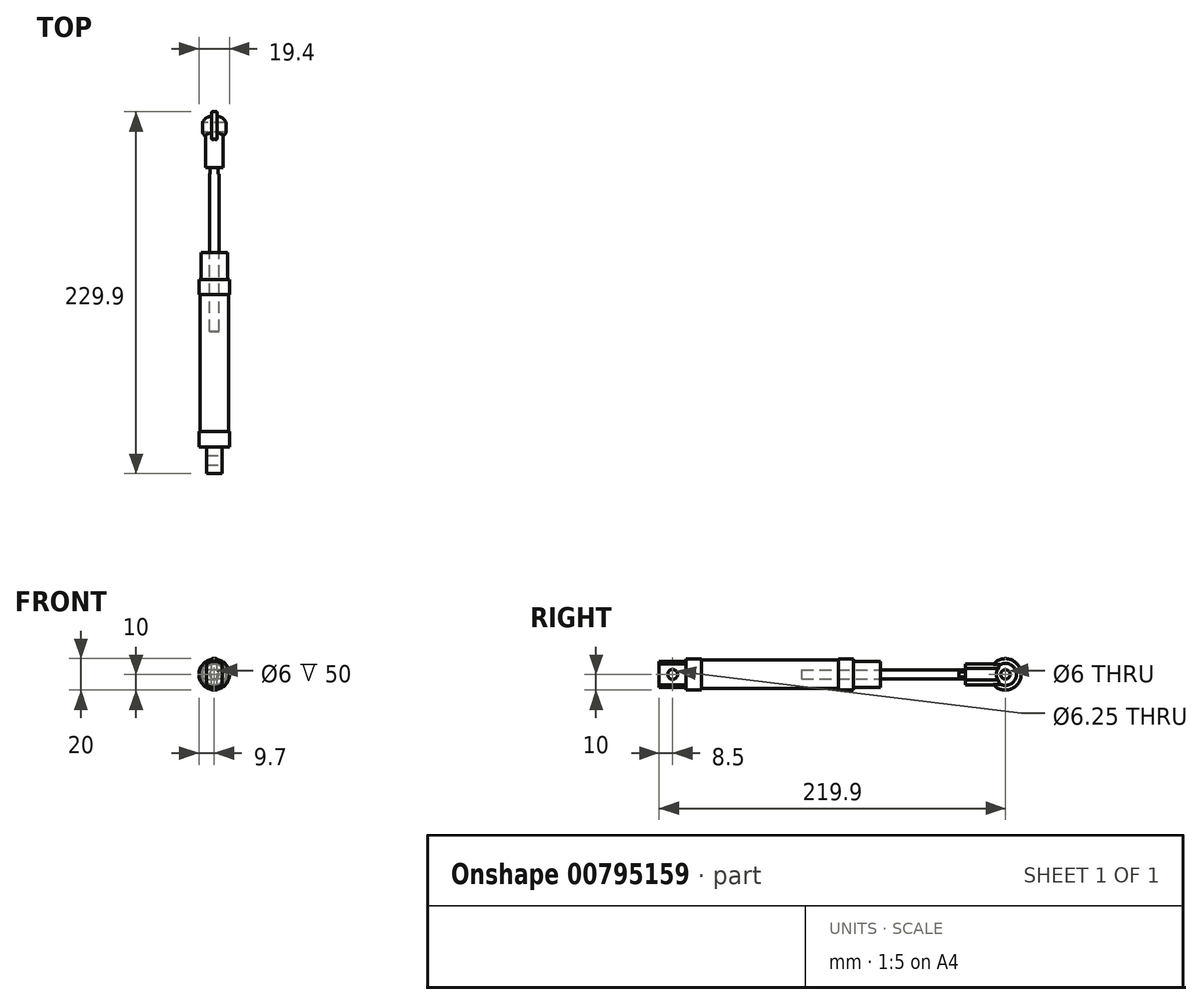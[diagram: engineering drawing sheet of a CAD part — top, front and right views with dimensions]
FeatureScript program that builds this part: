
annotation { "Feature Type Name" : "Feature", "Feature Type Description" : "" }
export const myFeature = defineFeature(function(context is Context, id is Id, definition is map)
    precondition{}
    {
        {
            var Q0;
            Q0=qCreatedBy(makeId("Front.planeOp"),FACE);
            var sketch = newSketch(context, id + "F0", { "sketchPlane" : qUnion([Q0])});
            skCircle(sketch, "E0", {"center": v(0, 0) * mm, "radius": 8.32 * mm});
            skSolve(sketch);
        }
        {
            var Q0;
            Q0=makeQuery(id+"F0.imprint","IMPRINT",FACE,{"disambiguationData":[TD([[makeQuery(id+"F0.imprint","IMPRINT",EDGE,{"derivedFrom":sQuery(id+"F0.wireOp",EDGE,"E0")}),1.0]])]});
            extrude(context, id + "F1", {"entities" : qUnion([Q0]), "depth" : 17 * mm, "offsetDistance" : 25 * mm});
        }
        {
            var Q0;
            Q0=makeQuery(id+"F1.opExtrude","CAP_FACE",FACE,{"disambiguationData":[OSD([sQuery(id+"F0.wireOp",EDGE,"E0")])],"isStart":false});
            var sketch = newSketch(context, id + "F2", { "sketchPlane" : qUnion([Q0])});
            skCircle(sketch, "E1", {"center": v(0, 0) * mm, "radius": 9.7 * mm});
            skSolve(sketch);
        }
        {
            var Q0;
            Q0=makeQuery(id+"F2.imprint","IMPRINT",FACE,{"disambiguationData":[TD([[makeQuery(id+"F2.imprint","IMPRINT",EDGE,{"derivedFrom":sQuery(id+"F2.wireOp",EDGE,"E1")}),1.0]])]});
            var Q1;
            Q1=makeQuery(id+"F2.imprint","IMPRINT",FACE,{"disambiguationData":[TD([[makeQuery(id+"F2.imprint","IMPRINT",EDGE,{"derivedFrom":makeQuery(id+"F1.opExtrude","CAP_EDGE",EDGE,{"disambiguationData":[OSD([sQuery(id+"F0.wireOp",EDGE,"E0")])],"isStart":false})}),1.0]])]});
            extrude(context, id + "F3", {"entities" : qUnion([Q0, Q1]), "operationType" : NewBodyOperationType.ADD, "depth" : 9.65 * mm, "offsetDistance" : 25 * mm});
        }
        {
            var Q0;
            Q0=makeQuery(id+"F3.opExtrude","CAP_FACE",FACE,{"disambiguationData":[OSD([sQuery(id+"F2.wireOp",EDGE,"E1")])],"isStart":false});
            var sketch = newSketch(context, id + "F4", { "sketchPlane" : qUnion([Q0])});
            skCircle(sketch, "E2", {"center": v(0, 0) * mm, "radius": 9.05 * mm});
            skSolve(sketch);
        }
        {
            var Q0;
            Q0=makeQuery(id+"F4.imprint","IMPRINT",FACE,{"disambiguationData":[TD([[makeQuery(id+"F4.imprint","IMPRINT",EDGE,{"derivedFrom":sQuery(id+"F4.wireOp",EDGE,"E2")}),1.0]])]});
            extrude(context, id + "F5", {"entities" : qUnion([Q0]), "operationType" : NewBodyOperationType.ADD, "depth" : 87 * mm, "offsetDistance" : 25 * mm});
        }
        {
            var Q0;
            Q0=makeQuery(id+"F5.opExtrude","CAP_FACE",FACE,{"disambiguationData":[OSD([sQuery(id+"F4.wireOp",EDGE,"E2")])],"isStart":false});
            var sketch = newSketch(context, id + "F6", { "sketchPlane" : qUnion([Q0])});
            skCircle(sketch, "E3", {"center": v(0, 0) * mm, "radius": 9.7 * mm});
            skSolve(sketch);
        }
        {
            var Q0;
            Q0=makeQuery(id+"F6.imprint","IMPRINT",FACE,{"disambiguationData":[TD([[makeQuery(id+"F6.imprint","IMPRINT",EDGE,{"derivedFrom":makeQuery(id+"F5.opExtrude","CAP_EDGE",EDGE,{"disambiguationData":[OSD([sQuery(id+"F4.wireOp",EDGE,"E2")])],"isStart":false})}),1.0]])]});
            var Q1;
            Q1=makeQuery(id+"F6.imprint","IMPRINT",FACE,{"disambiguationData":[TD([[makeQuery(id+"F6.imprint","IMPRINT",EDGE,{"derivedFrom":sQuery(id+"F6.wireOp",EDGE,"E3")}),1.0]])]});
            extrude(context, id + "F7", {"entities" : qUnion([Q0, Q1]), "operationType" : NewBodyOperationType.ADD, "depth" : 9.75 * mm, "offsetDistance" : 25 * mm});
        }
        {
            var Q0;
            Q0=makeQuery(id+"F7.opExtrude","CAP_FACE",FACE,{"disambiguationData":[OSD([sQuery(id+"F6.wireOp",EDGE,"E3")])],"isStart":false});
            var sketch = newSketch(context, id + "F8", { "sketchPlane" : qUnion([Q0])});
            skCircle(sketch, "E4", {"center": v(0, 0) * mm, "radius": 8.32 * mm});
            skSolve(sketch);
        }
        {
            var Q0;
            Q0=makeQuery(id+"F8.imprint","IMPRINT",FACE,{"disambiguationData":[TD([[makeQuery(id+"F8.imprint","IMPRINT",EDGE,{"derivedFrom":sQuery(id+"F8.wireOp",EDGE,"E4")}),1.0]])]});
            extrude(context, id + "F9", {"entities" : qUnion([Q0]), "operationType" : NewBodyOperationType.ADD, "depth" : 17 * mm, "offsetDistance" : 25 * mm});
        }
        {
            var Q0;
            Q0=makeQuery(id+"F1.opExtrude","CAP_FACE",FACE,{"disambiguationData":[OSD([sQuery(id+"F0.wireOp",EDGE,"E0")])],"isStart":true});
            var sketch = newSketch(context, id + "F10", { "sketchPlane" : qUnion([Q0])});
            skCircle(sketch, "E5", {"center": v(0, 0) * mm, "radius": 3 * mm});
            skSolve(sketch);
        }
        {
            var Q0;
            Q0=makeQuery(id+"F10.imprint","IMPRINT",FACE,{"disambiguationData":[TD([[makeQuery(id+"F10.imprint","IMPRINT",EDGE,{"derivedFrom":sQuery(id+"F10.wireOp",EDGE,"E5")}),1.0]])]});
            extrude(context, id + "F11", {"entities" : qUnion([Q0]), "operationType" : NewBodyOperationType.REMOVE, "oppositeDirection" : true, "depth" : 50 * mm, "offsetDistance" : 25 * mm});
        }
        {
            var Q0;
            Q0=makeQuery(id+"F1.opExtrude","CAP_FACE",FACE,{"disambiguationData":[OSD([sQuery(id+"F0.wireOp",EDGE,"E0")])],"isStart":true});
            var sketch = newSketch(context, id + "F12", { "sketchPlane" : qUnion([Q0])});
            skCircle(sketch, "E6", {"center": v(0, 0) * mm, "radius": 3 * mm});
            skSolve(sketch);
        }
        {
            var Q0;
            Q0=makeQuery(id+"F12.imprint","IMPRINT",FACE,{"disambiguationData":[TD([[makeQuery(id+"F12.imprint","IMPRINT",EDGE,{"derivedFrom":sQuery(id+"F12.wireOp",EDGE,"E6")}),1.0]])]});
            extrude(context, id + "F13", {"entities" : qUnion([Q0]), "depth" : 50 * mm, "offsetDistance" : 25 * mm});
        }
        {
            var Q0;
            Q0=makeQuery(id+"F13.opExtrude","CAP_FACE",FACE,{"disambiguationData":[OSD([sQuery(id+"F12.wireOp",EDGE,"E6")])],"isStart":false});
            var sketch = newSketch(context, id + "F14", { "sketchPlane" : qUnion([Q0])});
            skCircle(sketch, "E7", {"center": v(0, 0) * mm, "radius": 3 * mm});
            skLineSegment(sketch, "E8", {"start": v(-2.5, 1.65) * mm, "end": v(-2.5, -1.65) * mm});
            skLineSegment(sketch, "E9.MirrorCS", {"start": v(2.5, 1.65) * mm, "end": v(2.5, -1.65) * mm});
            skSolve(sketch);
        }
        {
            var Q0;
            {var subQ0=sQuery(id+"F14.wireOp",EDGE,"E8");Q0=makeQuery(id+"F14.imprint","IMPRINT",FACE,{"disambiguationData":[TD([[makeQuery(id+"F14.imprint","IMPRINT",EDGE,{"derivedFrom":subQ0}),1.0]])]});}
            extrude(context, id + "F15", {"entities" : qUnion([Q0]), "operationType" : NewBodyOperationType.ADD, "depth" : 4 * mm, "offsetDistance" : 25 * mm});
        }
        {
            var Q0;
            Q0=makeQuery(id+"F15.opExtrude","CAP_FACE",FACE,{"disambiguationData":[OSD([sQuery(id+"F14.wireOp",EDGE,"E7"),sQuery(id+"F14.wireOp",EDGE,"E8"),sQuery(id+"F14.wireOp",EDGE,"E9.MirrorCS")])],"isStart":false});
            var sketch = newSketch(context, id + "F16", { "sketchPlane" : qUnion([Q0])});
            skCircle(sketch, "E10", {"center": v(0, 0) * mm, "radius": 6.6 * mm});
            skLineSegment(sketch, "E11", {"start": v(-5.5, 3.65) * mm, "end": v(-5.5, -3.65) * mm});
            skLineSegment(sketch, "E12.MirrorCS", {"start": v(5.5, 3.65) * mm, "end": v(5.5, -3.65) * mm});
            skSolve(sketch);
        }
        {
            var Q0;
            {var subQ0=sQuery(id+"F16.wireOp",EDGE,"E11");Q0=makeQuery(id+"F16.imprint","IMPRINT",FACE,{"disambiguationData":[TD([[makeQuery(id+"F16.imprint","IMPRINT",EDGE,{"derivedFrom":subQ0}),1.0]])]});}
            var Q1;
            {var subQ0=sQuery(id+"F14.wireOp",EDGE,"E8");Q1=makeQuery(id+"F16.imprint","IMPRINT",FACE,{"disambiguationData":[TD([[makeQuery(id+"F16.imprint","IMPRINT",EDGE,{"derivedFrom":makeQuery(id+"F15.opExtrude","CAP_EDGE",EDGE,{"disambiguationData":[OSD([subQ0])],"isStart":false})}),1.0]])]});}
            extrude(context, id + "F17", {"entities" : qUnion([Q0, Q1]), "operationType" : NewBodyOperationType.ADD, "depth" : 22 * mm, "offsetDistance" : 25 * mm});
        }
        {
            var Q0;
            Q0=qCreatedBy(makeId("Right.planeOp"),FACE);
            var sketch = newSketch(context, id + "F18", { "sketchPlane" : qUnion([Q0])});
            skLineSegment(sketch, "E13.0", {"start": v(54, 3.65) * mm, "end": v(54, -3.65) * mm});
            skLineSegment(sketch, "E14", {"start": v(54, 0) * mm, "end": v(79.5, 0) * mm});
            skCircle(sketch, "E15", {"center": v(79.5, 0) * mm, "radius": 3 * mm});
            skCircle(sketch, "E16", {"center": v(79.5, 0) * mm, "radius": 7 * mm});
            skCircle(sketch, "E17", {"center": v(79.5, 0) * mm, "radius": 10 * mm});
            skSolve(sketch);
        }
        {
            var Q0;
            Q0=makeQuery(id+"F18.imprint","IMPRINT",FACE,{"disambiguationData":[TD([[makeQuery(id+"F18.imprint","IMPRINT",EDGE,{"derivedFrom":sQuery(id+"F18.wireOp",EDGE,"E16")}),-1.0]])]});
            var Q1;
            Q1=makeQuery(id+"F18.imprint","IMPRINT",FACE,{"disambiguationData":[TD([[makeQuery(id+"F18.imprint","IMPRINT",EDGE,{"derivedFrom":sQuery(id+"F18.wireOp",EDGE,"E15")}),-1.0]])]});
            extrude(context, id + "F19", {"entities" : qUnion([Q0, Q1]), "operationType" : NewBodyOperationType.ADD, "depth" : 1.75 * mm, "offsetDistance" : 25 * mm, "hasSecondDirection" : true, "secondDirectionOppositeDirection" : true, "secondDirectionDepth" : 1.75 * mm});
        }
        {
            var Q0;
            Q0=makeQuery(id+"F18.imprint","IMPRINT",FACE,{"disambiguationData":[TD([[makeQuery(id+"F18.imprint","IMPRINT",EDGE,{"derivedFrom":sQuery(id+"F18.wireOp",EDGE,"E15")}),-1.0]])]});
            extrude(context, id + "F20", {"entities" : qUnion([Q0]), "operationType" : NewBodyOperationType.ADD, "depth" : 7.5 * mm, "offsetDistance" : 25 * mm, "hasSecondDirection" : true, "secondDirectionOppositeDirection" : true, "secondDirectionDepth" : 7.5 * mm});
        }
        {
            var Q0;
            Q0=makeQuery(id+"F20.opExtrude","CAP_EDGE",EDGE,{"disambiguationData":[OSD([sQuery(id+"F18.wireOp",EDGE,"E16")])],"isStart":false});
            var Q1;
            Q1=makeQuery(id+"F20.opExtrude","CAP_EDGE",EDGE,{"disambiguationData":[OSD([sQuery(id+"F18.wireOp",EDGE,"E16")])],"isStart":true});
            fillet(context, id + "F21", {"entities" : qUnion([Q0, Q1]), "radius" : 6 * mm, "tangentPropagation" : true, "allowEdgeOverflow" : false});
        }
        {
            var Q0;
            Q0=makeQuery(id+"F19.opExtrude","CAP_EDGE",EDGE,{"disambiguationData":[OSD([sQuery(id+"F18.wireOp",EDGE,"E17")])],"isStart":false});
            var Q1;
            Q1=makeQuery(id+"F19.opExtrude","CAP_EDGE",EDGE,{"disambiguationData":[OSD([sQuery(id+"F18.wireOp",EDGE,"E17")])],"isStart":true});
            fillet(context, id + "F22", {"entities" : qUnion([Q0, Q1]), "radius" : .6 * mm, "tangentPropagation" : true, "allowEdgeOverflow" : false});
        }
        {
            var Q0;
            Q0=makeQuery(id+"F9.opExtrude","CAP_FACE",FACE,{"disambiguationData":[OSD([sQuery(id+"F8.wireOp",EDGE,"E4")])],"isStart":false});
            var sketch = newSketch(context, id + "F23", { "sketchPlane" : qUnion([Q0])});
            skLineSegment(sketch, "E18", {"start": v(-5, 6.66) * mm, "end": v(-5, -6.66) * mm});
            skLineSegment(sketch, "E19", {"start": v(5, 6.66) * mm, "end": v(5, -6.66) * mm});
            skSolve(sketch);
        }
        {
            var Q0;
            {var subQ0=sQuery(id+"F23.wireOp",EDGE,"E18");Q0=makeQuery(id+"F23.imprint","IMPRINT",FACE,{"disambiguationData":[TD([[makeQuery(id+"F23.imprint","IMPRINT",EDGE,{"derivedFrom":subQ0}),-1.0]])]});}
            var Q1;
            {var subQ0=sQuery(id+"F23.wireOp",EDGE,"E19");Q1=makeQuery(id+"F23.imprint","IMPRINT",FACE,{"disambiguationData":[TD([[makeQuery(id+"F23.imprint","IMPRINT",EDGE,{"derivedFrom":subQ0}),1.0]])]});}
            var Q2;
            Q2=makeQuery(id+"F7.opExtrude","CAP_FACE",FACE,{"disambiguationData":[OSD([sQuery(id+"F6.wireOp",EDGE,"E3")])],"isStart":false});
            extrude(context, id + "F24", {"entities" : qUnion([Q0, Q1]), "operationType" : NewBodyOperationType.REMOVE, "endBound" : BoundingType.UP_TO_SURFACE, "oppositeDirection" : true, "depth" : 18 * mm, "endBoundEntityFace" : qUnion([Q2]), "offsetDistance" : 25 * mm});
        }
        {
            var Q0;
            Q0=makeQuery(id+"F24.boolean.opBoolean","COPY",FACE,{"derivedFrom":makeQuery(id+"F24.opExtrude","SWEPT_FACE",FACE,{"disambiguationData":[OSD([sQuery(id+"F23.wireOp",EDGE,"E19")])]})});
            var sketch = newSketch(context, id + "F25", { "sketchPlane" : qUnion([Q0])});
            skCircle(sketch, "E20", {"center": v(-131.9, 0) * mm, "radius": 3.12 * mm});
            skPoint(sketch, "E20.centerSnap0", {"position": v(-131.9, 6.66) * mm});
            skPoint(sketch, "E20.centerSnap1", {"position": v(-123.4, 0) * mm});
            skSolve(sketch);
        }
        {
            var Q0;
            Q0=makeQuery(id+"F25.imprint","IMPRINT",FACE,{"disambiguationData":[TD([[makeQuery(id+"F25.imprint","IMPRINT",EDGE,{"derivedFrom":sQuery(id+"F25.wireOp",EDGE,"E20")}),1.0]])]});
            extrude(context, id + "F26", {"entities" : qUnion([Q0]), "operationType" : NewBodyOperationType.REMOVE, "endBound" : BoundingType.THROUGH_ALL, "oppositeDirection" : true, "depth" : 25 * mm, "offsetDistance" : 25 * mm});
        }
    });
